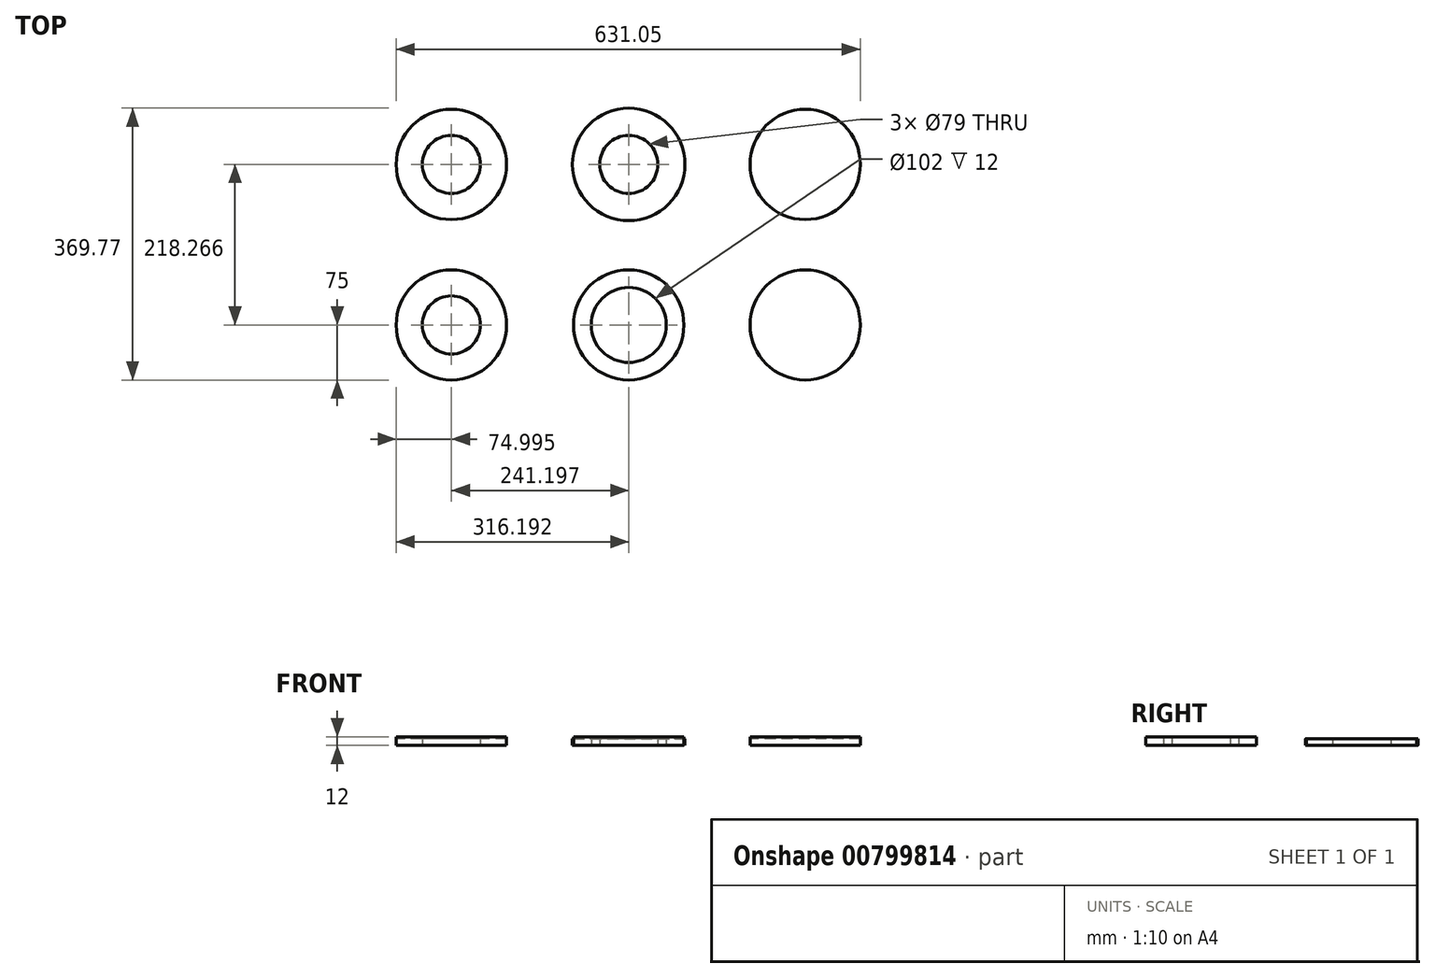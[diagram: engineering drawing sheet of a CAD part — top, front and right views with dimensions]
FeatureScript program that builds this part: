
annotation { "Feature Type Name" : "Feature", "Feature Type Description" : "" }
export const myFeature = defineFeature(function(context is Context, id is Id, definition is map)
    precondition{}
    {
        {
            var Q0;
            Q0=qCreatedBy(makeId("Top.planeOp"),FACE);
            var sketch = newSketch(context, id + "F0", { "sketchPlane" : qUnion([Q0])});
            skCircle(sketch, "E0", {"center": v(-188.48, 0) * mm, "radius": 75 * mm});
            skCircle(sketch, "E1", {"center": v(-188.48, 0) * mm, "radius": 39.5 * mm});
            skSolve(sketch);
        }
        {
            var Q0;
            Q0 = qSketchRegion(id + "F0", true);
            extrude(context, id + "F1", {"entities" : qUnion([Q0]), "depth" : 12 * mm, "offsetDistance" : 25 * mm});
        }
        {
            var Q0;
            Q0=qCreatedBy(makeId("Top.planeOp"),FACE);
            var sketch = newSketch(context, id + "F2", { "sketchPlane" : qUnion([Q0])});
            skCircle(sketch, "E2", {"center": v(52.71, 0) * mm, "radius": 75 * mm});
            skCircle(sketch, "E3", {"center": v(52.71, 0) * mm, "radius": 51 * mm});
            skSolve(sketch);
        }
        {
            var Q0;
            Q0 = qSketchRegion(id + "F2", true);
            extrude(context, id + "F3", {"entities" : qUnion([Q0]), "depth" : 12 * mm, "offsetDistance" : 25 * mm});
        }
        {
            var Q0;
            Q0=qCreatedBy(makeId("Top.planeOp"),FACE);
            var sketch = newSketch(context, id + "F4", { "sketchPlane" : qUnion([Q0])});
            skCircle(sketch, "E4", {"center": v(-188.48, 218.27) * mm, "radius": 75 * mm});
            skCircle(sketch, "E5", {"center": v(-188.48, 218.27) * mm, "radius": 39.5 * mm});
            skSolve(sketch);
        }
        {
            var Q0;
            Q0 = qSketchRegion(id + "F4", true);
            extrude(context, id + "F5", {"entities" : qUnion([Q0]), "depth" : 9 * mm, "offsetDistance" : 25 * mm});
        }
        {
            var Q0;
            Q0=qCreatedBy(makeId("Top.planeOp"),FACE);
            var sketch = newSketch(context, id + "F6", { "sketchPlane" : qUnion([Q0])});
            skCircle(sketch, "E6", {"center": v(292.57, 0) * mm, "radius": 75 * mm});
            skSolve(sketch);
        }
        {
            var Q0;
            Q0=makeQuery(id+"F6.imprint","IMPRINT",FACE,{"disambiguationData":[TD([[makeQuery(id+"F6.imprint","IMPRINT",EDGE,{"derivedFrom":sQuery(id+"F6.wireOp",EDGE,"E6")}),1.0]])]});
            extrude(context, id + "F7", {"entities" : qUnion([Q0]), "depth" : 12 * mm, "offsetDistance" : 25 * mm});
        }
        {
            var Q0;
            Q0=qCreatedBy(makeId("Top.planeOp"),FACE);
            var sketch = newSketch(context, id + "F8", { "sketchPlane" : qUnion([Q0])});
            skCircle(sketch, "E7", {"center": v(52.71, 218.27) * mm, "radius": 76.5 * mm});
            skCircle(sketch, "E8", {"center": v(52.71, 218.27) * mm, "radius": 39.5 * mm});
            skSolve(sketch);
        }
        {
            var Q0;
            Q0 = qSketchRegion(id + "F8", true);
            extrude(context, id + "F9", {"entities" : qUnion([Q0]), "depth" : 9 * mm, "offsetDistance" : 25 * mm});
        }
        {
            var Q0;
            Q0=qCreatedBy(makeId("Top.planeOp"),FACE);
            var sketch = newSketch(context, id + "F10", { "sketchPlane" : qUnion([Q0])});
            skCircle(sketch, "E9", {"center": v(292.57, 218.27) * mm, "radius": 75 * mm});
            skSolve(sketch);
        }
        {
            var Q0;
            Q0 = qSketchRegion(id + "F10", true);
            extrude(context, id + "F11", {"entities" : qUnion([Q0]), "depth" : 9 * mm, "offsetDistance" : 25 * mm});
        }
    });
